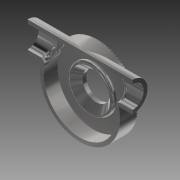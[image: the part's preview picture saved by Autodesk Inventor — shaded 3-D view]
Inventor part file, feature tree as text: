
AUTODESK INVENTOR PART (.ipt)
format: ipt  version: 2021 (Build 250183000, 183)  size: 712,192 bytes
history: native  units: mm
features: sketch x5, other x3, fillet x3, revolve x2, extrude x2, plane x1, pattern_circular x1
ambient origin geometry x8: Origin, YZ Plane, XZ Plane, XY Plane, X Axis, Y Axis, Z Axis, Center Point
bodies: Body1 (feature_tree)
feature tree (17):
  other  "Sólido1"
  sketch  "Boceto1"  dims[d0=0.5mm d8=7.0mm d9=6.0mm]
  revolve  "Revolución1"  [1 undecoded]
  fillet  "Empalme1"  Radius=6.0mm
  plane  "Plano de trabajo1"
  sketch  "Boceto2"  dims[d10=1.5mm d11=4.5mm]
  extrude  "Extrusión2"  Depth=4.5mm
  other  "Suprimir cara1"
  revolve  "Revolución2"  Angle=90.0deg
  fillet  "Empalme5"  Radius=2.0mm
  extrude  "Extrusión3"  Depth=1.0mm
  pattern_circular  "Patrón circular2"  [2 undecoded]
  fillet  "Empalme7"  Radius=6.0mm
  other  "Suprimir cara3"
  sketch  "Boceto5"  dims[d18=-8.0mm d20=1.0mm]
  sketch  "Boceto6"  dims[d21=0.5mm d23=0.5mm d30=6.0mm d37=1.5mm d38=9.0mm d39=42.0mm d40=0.0mm d42=90.0deg d44=2.0mm d46=42.0mm d47=0.0mm d48=940.0mm d49=360.0deg d60=1.0mm d61=1.5mm]
  sketch  "Boceto3"  dims[d13=1.5mm d15=90.0deg d16=2.0mm]
note: 3 required parameter values undecoded (feature->parameter linkage not recoverable at this tier; creation-order binding heuristic only, values carry confidence <= 0.55)